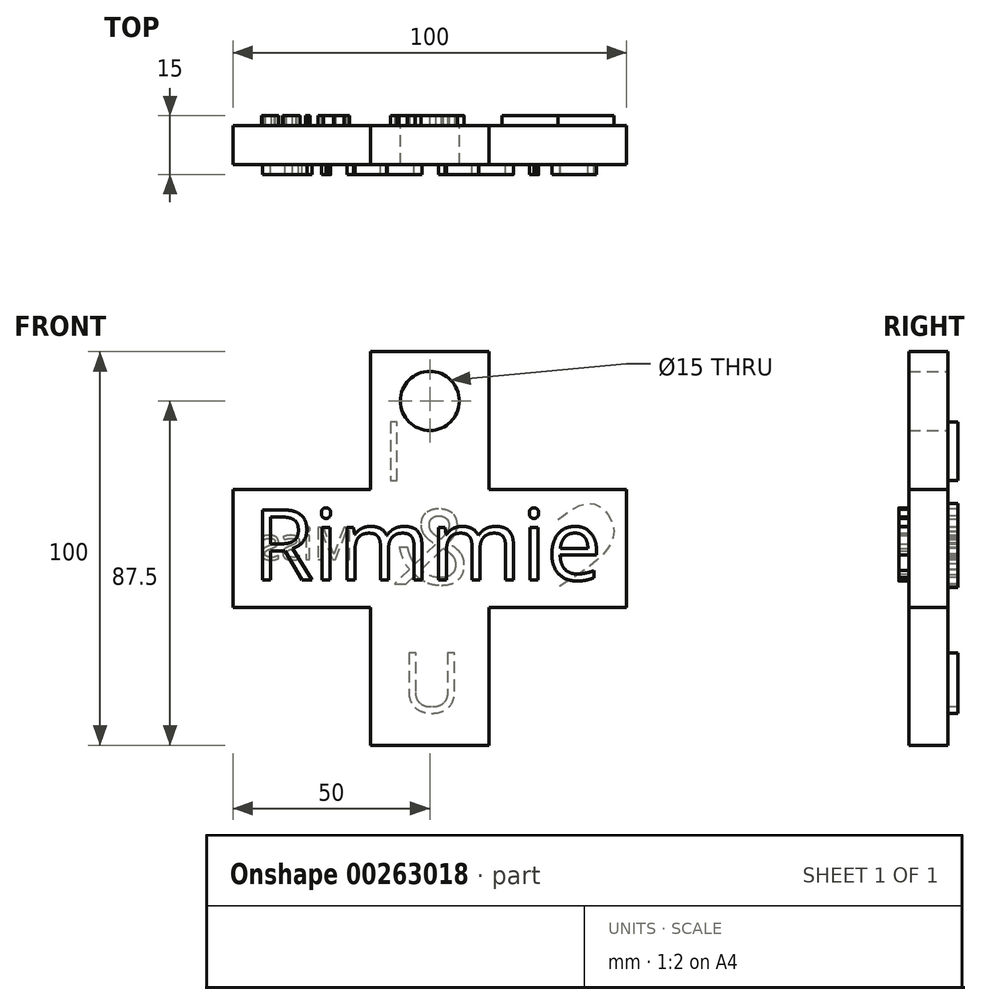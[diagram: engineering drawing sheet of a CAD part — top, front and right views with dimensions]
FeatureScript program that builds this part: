
annotation { "Feature Type Name" : "Feature", "Feature Type Description" : "" }
export const myFeature = defineFeature(function(context is Context, id is Id, definition is map)
    precondition{}
    {
        {
            var Q0;
            Q0=qCreatedBy(makeId("Front.planeOp"),FACE);
            var sketch = newSketch(context, id + "F0", { "sketchPlane" : qUnion([Q0])});
            skPoint(sketch, "E0.middle", {"position": v(0, 0) * mm});
            skLineSegment(sketch, "E1.bottom", {"start": v(50, -15) * mm, "end": v(-50, -15) * mm});
            skLineSegment(sketch, "E1.top", {"start": v(50, 15) * mm, "end": v(-50, 15) * mm});
            skLineSegment(sketch, "E1.left", {"start": v(50, -15) * mm, "end": v(50, 15) * mm});
            skLineSegment(sketch, "E1.right", {"start": v(-50, -15) * mm, "end": v(-50, 15) * mm});
            skLineSegment(sketch, "E2.bottom", {"start": v(15, -50) * mm, "end": v(-15, -50) * mm});
            skLineSegment(sketch, "E2.top", {"start": v(15, 50) * mm, "end": v(-15, 50) * mm});
            skLineSegment(sketch, "E2.left", {"start": v(15, -50) * mm, "end": v(15, 50) * mm});
            skLineSegment(sketch, "E2.right", {"start": v(-15, -50) * mm, "end": v(-15, 50) * mm});
            skCircle(sketch, "E3", {"center": v(0, 37.5) * mm, "radius": 7.5 * mm});
            skSolve(sketch);
        }
        {
            var Q0;
            Q0 = qSketchRegion(id + "F0", true);
            extrude(context, id + "F1", {"entities" : qUnion([Q0]), "depth" : 10 * mm});
        }
        {
            var Q0;
            Q0=makeQuery(id+"F1.opExtrude","CAP_FACE",FACE,{"disambiguationData":[OSD([sQuery(id+"F0.wireOp",EDGE,"E1.bottom"),sQuery(id+"F0.wireOp",EDGE,"E1.top"),sQuery(id+"F0.wireOp",EDGE,"E1.left"),sQuery(id+"F0.wireOp",EDGE,"E1.right"),sQuery(id+"F0.wireOp",EDGE,"E2.bottom"),sQuery(id+"F0.wireOp",EDGE,"E2.top"),sQuery(id+"F0.wireOp",EDGE,"E2.left"),sQuery(id+"F0.wireOp",EDGE,"E2.right")])],"isStart":false});
            var sketch = newSketch(context, id + "F2", { "sketchPlane" : qUnion([Q0])});
            skText(sketch, "E4", { "text": "Rimmie", "fontName": "OpenSans-Regular.ttf"});
            const initialGuessF2  = {"E4": [-0.045, -0.008, 1, 0, 0.018]};
            skSetInitialGuess(sketch, initialGuessF2);
            skSolve(sketch);
        }
        {
            var Q0;
            Q0 = qSketchRegion(id + "F2", true);
            extrude(context, id + "F3", {"entities" : qUnion([Q0]), "operationType" : NewBodyOperationType.ADD, "depth" : 2.5 * mm});
        }
        {
            var Q0;
            Q0=makeQuery(id+"F1.opExtrude","CAP_FACE",FACE,{"disambiguationData":[OSD([sQuery(id+"F0.wireOp",EDGE,"E1.bottom"),sQuery(id+"F0.wireOp",EDGE,"E1.top"),sQuery(id+"F0.wireOp",EDGE,"E1.left"),sQuery(id+"F0.wireOp",EDGE,"E1.right"),sQuery(id+"F0.wireOp",EDGE,"E2.bottom"),sQuery(id+"F0.wireOp",EDGE,"E2.top"),sQuery(id+"F0.wireOp",EDGE,"E2.left"),sQuery(id+"F0.wireOp",EDGE,"E2.right")])],"isStart":true});
            var sketch = newSketch(context, id + "F4", { "sketchPlane" : qUnion([Q0])});
            skText(sketch, "E5", { "text": "I", "fontName": "OpenSans-Regular.ttf"});
            skText(sketch, "E6", { "text": "U", "fontName": "OpenSans-Regular.ttf"});
            const initialGuessF4  = {"E5": [0.00625, 0.01733, 1, 0, 0.015], "E6": [-0.00821, -0.04164, 1, 0, 0.0153]};
            skSetInitialGuess(sketch, initialGuessF4);
            skSolve(sketch);
        }
        {
            var Q0;
            Q0=makeQuery(id+"F1.opExtrude","CAP_FACE",FACE,{"disambiguationData":[OSD([sQuery(id+"F0.wireOp",EDGE,"E1.bottom"),sQuery(id+"F0.wireOp",EDGE,"E1.top"),sQuery(id+"F0.wireOp",EDGE,"E1.left"),sQuery(id+"F0.wireOp",EDGE,"E1.right"),sQuery(id+"F0.wireOp",EDGE,"E2.bottom"),sQuery(id+"F0.wireOp",EDGE,"E2.top"),sQuery(id+"F0.wireOp",EDGE,"E2.left"),sQuery(id+"F0.wireOp",EDGE,"E2.right")])],"isStart":true});
            var sketch = newSketch(context, id + "F5", { "sketchPlane" : qUnion([Q0])});
            skText(sketch, "E7", { "text": "&", "fontName": "OpenSans-Regular.ttf"});
            const initialGuessF5  = {"E7": [-0.0102, -0.00906, 1, 0, 0.01898]};
            skSetInitialGuess(sketch, initialGuessF5);
            skSolve(sketch);
        }
        {
            var Q0;
            Q0 = qSketchRegion(id + "F5", true);
            extrude(context, id + "F6", {"entities" : qUnion([Q0]), "operationType" : NewBodyOperationType.ADD, "depth" : 2.5 * mm});
        }
        {
            var Q0;
            {var subQ0=sQuery(id+"F0.wireOp",EDGE,"E2.left");var subQ1=sQuery(id+"F0.wireOp",EDGE,"E2.top");var subQ2=sQuery(id+"F0.wireOp",EDGE,"E1.top");var subQ4=sQuery(id+"F0.wireOp",EDGE,"E2.bottom");var subQ5=sQuery(id+"F0.wireOp",EDGE,"E1.right");var subQ6=sQuery(id+"F0.wireOp",EDGE,"E1.left");var subQ7=sQuery(id+"F0.wireOp",EDGE,"E1.bottom");var subQ9=sQuery(id+"F0.wireOp",EDGE,"E2.right");Q0=makeQuery(id+"F6.boolean.opBoolean","SPLIT",FACE,{"disambiguationData":[TD([makeQuery(id+"F1.opExtrude","SWEPT_FACE",FACE,{"disambiguationData":[OSD([subQ6])]})])],"derivedFrom":makeQuery(id+"F1.opExtrude","CAP_FACE",FACE,{"disambiguationData":[OSD([subQ7,subQ2,subQ6,subQ5,subQ4,subQ1,subQ0,subQ9])],"isStart":true})});}
            var sketch = newSketch(context, id + "F7", { "sketchPlane" : qUnion([Q0])});
            skText(sketch, "E8", { "text": "Miss", "fontName": "OpenSans-Regular.ttf"});
            const initialGuessF7  = {"E8": [0.01926, -0.00283, 1, 0, 0.00821]};
            skSetInitialGuess(sketch, initialGuessF7);
            skSolve(sketch);
        }
        {
            var Q0;
            Q0 = qSketchRegion(id + "F7", true);
            extrude(context, id + "F8", {"entities" : qUnion([Q0]), "operationType" : NewBodyOperationType.ADD, "depth" : 2.5 * mm});
        }
        {
            var Q0;
            {var subQ0=sQuery(id+"F0.wireOp",EDGE,"E2.left");var subQ1=sQuery(id+"F0.wireOp",EDGE,"E2.top");var subQ2=sQuery(id+"F0.wireOp",EDGE,"E1.top");var subQ4=sQuery(id+"F0.wireOp",EDGE,"E2.bottom");var subQ5=sQuery(id+"F0.wireOp",EDGE,"E1.right");var subQ6=sQuery(id+"F0.wireOp",EDGE,"E1.left");var subQ7=sQuery(id+"F0.wireOp",EDGE,"E1.bottom");var subQ9=sQuery(id+"F0.wireOp",EDGE,"E2.right");Q0=makeQuery(id+"F6.boolean.opBoolean","SPLIT",FACE,{"disambiguationData":[TD([makeQuery(id+"F1.opExtrude","SWEPT_FACE",FACE,{"disambiguationData":[OSD([subQ6])]})])],"derivedFrom":makeQuery(id+"F1.opExtrude","CAP_FACE",FACE,{"disambiguationData":[OSD([subQ7,subQ2,subQ6,subQ5,subQ4,subQ1,subQ0,subQ9])],"isStart":true})});}
            var sketch = newSketch(context, id + "F9", { "sketchPlane" : qUnion([Q0])});
            skFitSpline(sketch, "E9", {"points": [v(-32.58, 7.37) * mm, v(-41.64, 11.33) * mm, v(-46.74, 3.68) * mm, v(-32.58, -9.91) * mm], "startDerivative": vector(-31.17, 23.81) * mm, "endDerivative": vector(49.1, -31.29) * mm});
            skFitSpline(sketch, "E10.MirrorCS", {"points": [v(-32.58, 7.37) * mm, v(-23.51, 11.33) * mm, v(-18.41, 3.68) * mm, v(-32.58, -9.91) * mm], "startDerivative": vector(31.17, 23.81) * mm, "endDerivative": vector(-49.1, -31.29) * mm});
            skSolve(sketch);
        }
        {
            var Q0;
            Q0 = qSketchRegion(id + "F9", true);
            extrude(context, id + "F10", {"entities" : qUnion([Q0]), "operationType" : NewBodyOperationType.ADD, "depth" : 2.5 * mm});
        }
        {
            var Q0;
            Q0 = qSketchRegion(id + "F4", true);
            extrude(context, id + "F11", {"entities" : qUnion([Q0]), "operationType" : NewBodyOperationType.ADD, "depth" : 2.5 * mm});
        }
    });
